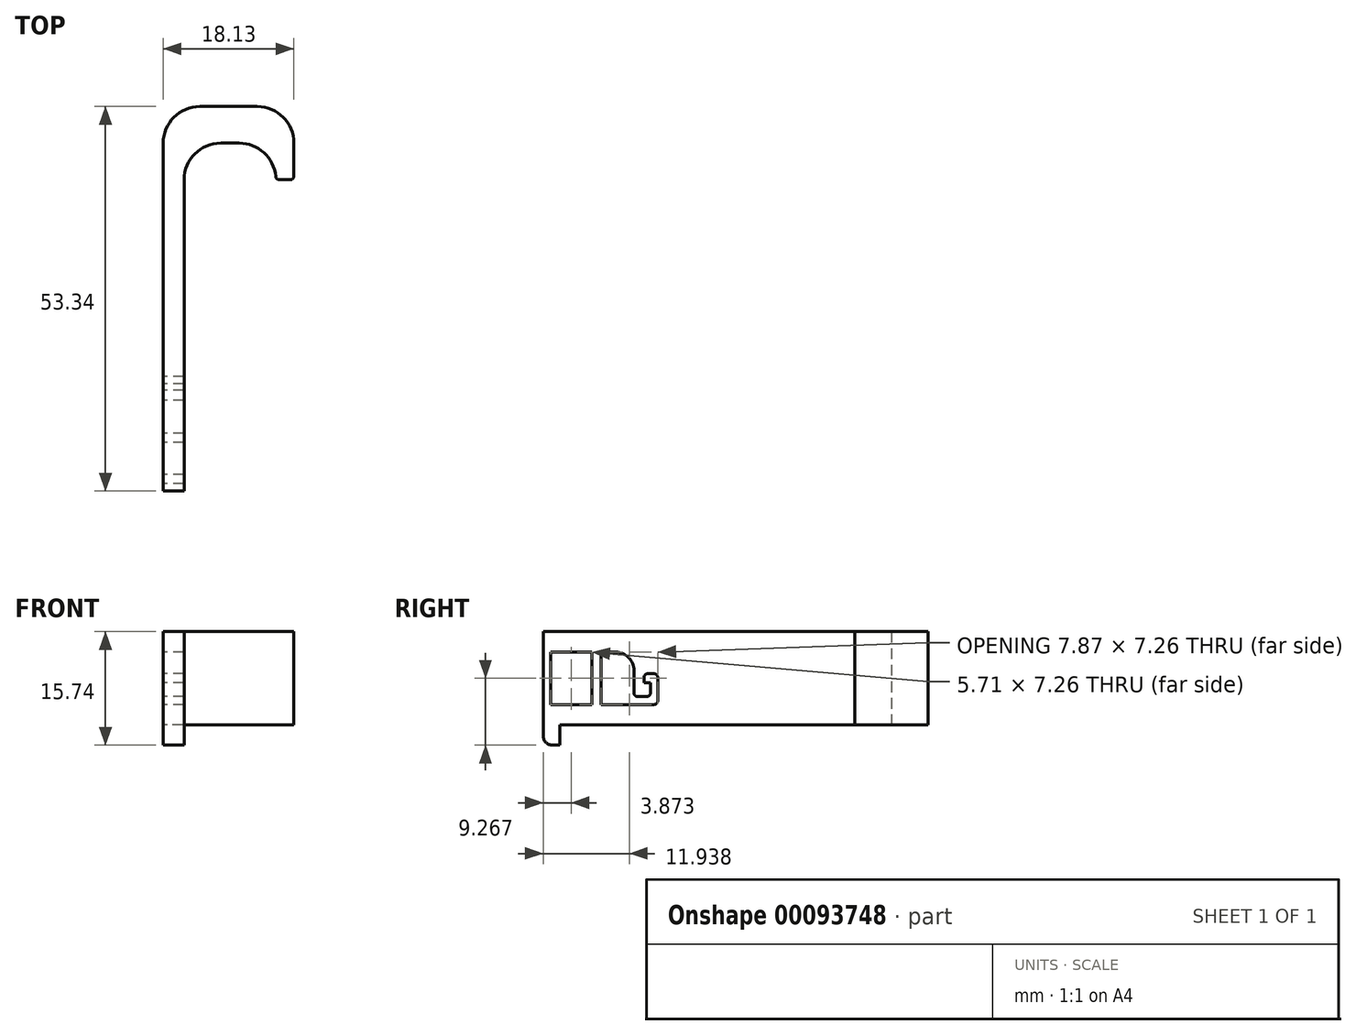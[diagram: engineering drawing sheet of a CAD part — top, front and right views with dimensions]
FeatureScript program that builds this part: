
annotation { "Feature Type Name" : "Feature", "Feature Type Description" : "" }
export const myFeature = defineFeature(function(context is Context, id is Id, definition is map)
    precondition{}
    {
        {
            var Q0;
            Q0=qCreatedBy(makeId("Top.planeOp"),FACE);
            var sketch = newSketch(context, id + "F0", { "sketchPlane" : qUnion([Q0])});
            skLineSegment(sketch, "E0", {"start": v(0, 0) * mm, "end": v(0, 48.26) * mm});
            skLineSegment(sketch, "E1", {"start": v(0, 0) * mm, "end": v(2.9, 0) * mm});
            skLineSegment(sketch, "E2", {"start": v(2.9, 0) * mm, "end": v(2.9, 43.18) * mm});
            skLineSegment(sketch, "E3", {"start": v(7.98, 48.26) * mm, "end": v(10.54, 48.26) * mm});
            skLineSegment(sketch, "E4", {"start": v(15.62, 43.18) * mm, "end": v(15.62, 43.18) * mm});
            skLineSegment(sketch, "E5", {"start": v(16.1, 43.18) * mm, "end": v(17.62, 43.18) * mm});
            skLineSegment(sketch, "E6", {"start": v(18.13, 43.69) * mm, "end": v(18.13, 48.26) * mm});
            skLineSegment(sketch, "E7", {"start": v(13.05, 53.34) * mm, "end": v(5.08, 53.34) * mm});
            skPoint(sketch, "E8.visualSharp", {"position": v(2.9, 48.26) * mm});
            skArc(sketch, "E8.filletArc", {"start": v(7.98, 48.26) * mm, "mid": v(4.38, 46.77) * mm, "end": v(2.9, 43.18) * mm});
            skPoint(sketch, "E9.visualSharp", {"position": v(15.62, 48.26) * mm});
            skArc(sketch, "E9.filletArc", {"start": v(15.6, 43.64) * mm, "mid": v(13.96, 46.93) * mm, "end": v(10.54, 48.26) * mm});
            skPoint(sketch, "E10.visualSharp", {"position": v(18.13, 53.34) * mm});
            skArc(sketch, "E10.filletArc", {"start": v(18.13, 48.26) * mm, "mid": v(16.64, 51.85) * mm, "end": v(13.05, 53.34) * mm});
            skPoint(sketch, "E11.visualSharp", {"position": v(0, 53.34) * mm});
            skArc(sketch, "E11.filletArc", {"start": v(5.08, 53.34) * mm, "mid": v(1.49, 51.85) * mm, "end": v(0, 48.26) * mm});
            skPoint(sketch, "E12.visualSharp", {"position": v(18.13, 43.18) * mm});
            skArc(sketch, "E12.filletArc", {"start": v(17.62, 43.18) * mm, "mid": v(17.98, 43.33) * mm, "end": v(18.13, 43.69) * mm});
            skPoint(sketch, "E13.visualSharp", {"position": v(15.62, 43.18) * mm});
            skArc(sketch, "E13.filletArc", {"start": v(15.6, 43.64) * mm, "mid": v(15.76, 43.31) * mm, "end": v(16.1, 43.18) * mm});
            skSolve(sketch);
        }
        {
            var Q0;
            Q0 = qSketchRegion(id + "F0", true);
            extrude(context, id + "F1", {"entities" : qUnion([Q0]), "depth" : 12.95 * mm});
        }
        {
            var Q0;
            Q0=makeQuery(id+"F1.opExtrude","SWEPT_FACE",FACE,{"disambiguationData":[OSD([sQuery(id+"F0.wireOp",EDGE,"E0")])]});
            var sketch = newSketch(context, id + "F2", { "sketchPlane" : qUnion([Q0])});
            skLineSegment(sketch, "E14", {"start": v(-15.37, 2.84) * mm, "end": v(-8, 2.84) * mm});
            skLineSegment(sketch, "E15", {"start": v(-1.02, 2.84) * mm, "end": v(-1.02, 10.1) * mm});
            skLineSegment(sketch, "E16", {"start": v(-1.02, 10.1) * mm, "end": v(-6.73, 10.1) * mm});
            skLineSegment(sketch, "E17", {"start": v(-12.57, 7.57) * mm, "end": v(-12.57, 4.44) * mm});
            skLineSegment(sketch, "E18", {"start": v(-13.08, 3.94) * mm, "end": v(-14.35, 3.94) * mm});
            skLineSegment(sketch, "E19", {"start": v(-14.86, 4.44) * mm, "end": v(-14.86, 5.84) * mm});
            skLineSegment(sketch, "E20", {"start": v(-14.86, 5.84) * mm, "end": v(-13.97, 5.84) * mm});
            skLineSegment(sketch, "E21", {"start": v(-13.97, 5.84) * mm, "end": v(-13.97, 6.6) * mm});
            skLineSegment(sketch, "E22", {"start": v(-14.48, 7.11) * mm, "end": v(-15.37, 7.11) * mm});
            skLineSegment(sketch, "E23", {"start": v(-15.88, 6.6) * mm, "end": v(-15.88, 3.35) * mm});
            skPoint(sketch, "E24", {"position": v(-13.97, 6.48) * mm});
            skPoint(sketch, "E25.visualSharp", {"position": v(-15.88, 2.84) * mm});
            skArc(sketch, "E25.filletArc", {"start": v(-15.88, 3.35) * mm, "mid": v(-15.73, 3) * mm, "end": v(-15.37, 2.84) * mm});
            skPoint(sketch, "E26.visualSharp", {"position": v(-15.88, 7.11) * mm});
            skArc(sketch, "E26.filletArc", {"start": v(-15.37, 7.11) * mm, "mid": v(-15.73, 6.96) * mm, "end": v(-15.88, 6.6) * mm});
            skPoint(sketch, "E27.visualSharp", {"position": v(-13.97, 7.11) * mm});
            skArc(sketch, "E27.filletArc", {"start": v(-13.97, 6.6) * mm, "mid": v(-14.12, 6.96) * mm, "end": v(-14.48, 7.11) * mm});
            skPoint(sketch, "E28.visualSharp", {"position": v(-14.86, 3.94) * mm});
            skArc(sketch, "E28.filletArc", {"start": v(-14.86, 4.44) * mm, "mid": v(-14.71, 4.09) * mm, "end": v(-14.35, 3.94) * mm});
            skPoint(sketch, "E29.visualSharp", {"position": v(-12.57, 10.1) * mm});
            skArc(sketch, "E29.filletArc", {"start": v(-10.03, 10.1) * mm, "mid": v(-11.83, 9.37) * mm, "end": v(-12.57, 7.57) * mm});
            skPoint(sketch, "E30.visualSharp", {"position": v(-12.57, 3.94) * mm});
            skArc(sketch, "E30.filletArc", {"start": v(-13.08, 3.94) * mm, "mid": v(-12.72, 4.09) * mm, "end": v(-12.57, 4.44) * mm});
            skLineSegment(sketch, "E31", {"start": v(-8, 2.84) * mm, "end": v(-8, 10.1) * mm});
            skLineSegment(sketch, "E32", {"start": v(-6.73, 2.84) * mm, "end": v(-6.73, 10.1) * mm});
            skLineSegment(sketch, "E33.trimOffspring", {"start": v(-6.73, 2.84) * mm, "end": v(-1.02, 2.84) * mm});
            skLineSegment(sketch, "E34.trimOffspring", {"start": v(-8, 10.1) * mm, "end": v(-10.03, 10.1) * mm});
            skSolve(sketch);
        }
        {
            var Q0;
            Q0 = qSketchRegion(id + "F2", true);
            extrude(context, id + "F3", {"entities" : qUnion([Q0]), "operationType" : NewBodyOperationType.REMOVE, "endBound" : BoundingType.THROUGH_ALL, "oppositeDirection" : true, "depth" : 25.4 * mm});
        }
        {
            var Q0;
            Q0=qCreatedBy(makeId("Right.planeOp"),FACE);
            var sketch = newSketch(context, id + "F4", { "sketchPlane" : qUnion([Q0])});
            skLineSegment(sketch, "E35", {"start": v(0, 0) * mm, "end": v(0, -1.52) * mm});
            skLineSegment(sketch, "E36", {"start": v(1.27, -2.8) * mm, "end": v(2.29, -2.8) * mm});
            skLineSegment(sketch, "E37", {"start": v(2.29, -2.8) * mm, "end": v(2.29, 0) * mm});
            skLineSegment(sketch, "E38", {"start": v(2.29, 0) * mm, "end": v(0, 0) * mm});
            skPoint(sketch, "E39.visualSharp", {"position": v(0, -2.8) * mm});
            skArc(sketch, "E39.filletArc", {"start": v(0, -1.52) * mm, "mid": v(0.37, -2.42) * mm, "end": v(1.27, -2.8) * mm});
            skSolve(sketch);
        }
        {
            var Q0;
            Q0 = qSketchRegion(id + "F4", true);
            var Q1;
            Q1=makeQuery(id+"F1.opExtrude","SWEPT_FACE",FACE,{"disambiguationData":[OSD([sQuery(id+"F0.wireOp",EDGE,"E2")])]});
            extrude(context, id + "F5", {"entities" : qUnion([Q0]), "operationType" : NewBodyOperationType.ADD, "endBound" : BoundingType.UP_TO_SURFACE, "endBoundEntityFace" : qUnion([Q1]), "depth" : 25.4 * mm});
        }
    });
